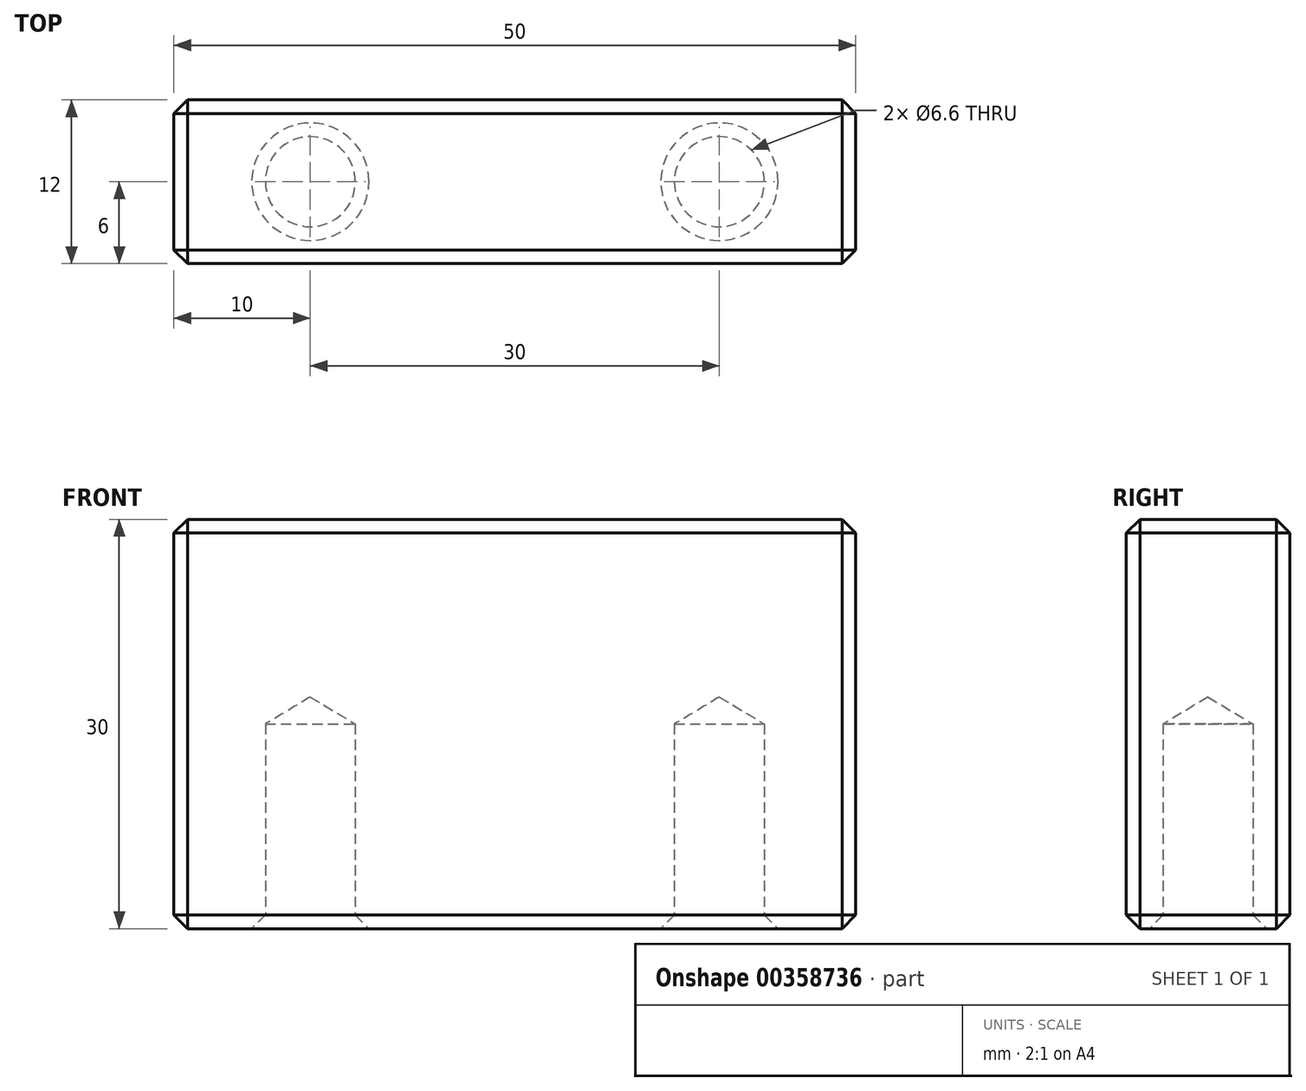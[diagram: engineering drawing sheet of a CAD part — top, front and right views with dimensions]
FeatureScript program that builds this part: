
annotation { "Feature Type Name" : "Feature", "Feature Type Description" : "" }
export const myFeature = defineFeature(function(context is Context, id is Id, definition is map)
    precondition{}
    {
        {
            var Q0;
            Q0=qCreatedBy(makeId("Front.planeOp"),FACE);
            var sketch = newSketch(context, id + "F0", { "sketchPlane" : qUnion([Q0])});
            skLineSegment(sketch, "E0.bottom", {"start": v(25, -15) * mm, "end": v(-25, -15) * mm});
            skLineSegment(sketch, "E0.top", {"start": v(25, 15) * mm, "end": v(-25, 15) * mm});
            skLineSegment(sketch, "E0.left", {"start": v(25, -15) * mm, "end": v(25, 15) * mm});
            skLineSegment(sketch, "E0.right", {"start": v(-25, -15) * mm, "end": v(-25, 15) * mm});
            skPoint(sketch, "E0.middle", {"position": v(0, 0) * mm});
            skSolve(sketch);
        }
        {
            var Q0;
            Q0=makeQuery(id+"F0.imprint","IMPRINT",FACE,{"disambiguationData":[TD([[makeQuery(id+"F0.imprint","IMPRINT",EDGE,{"derivedFrom":sQuery(id+"F0.wireOp",EDGE,"E0.bottom")}),-1.0]])]});
            extrude(context, id + "F1", {"entities" : qUnion([Q0]), "endBound" : BoundingType.SYMMETRIC, "depth" : 12 * mm});
        }
        {
            var Q0;
            Q0=makeQuery(id+"F1.opExtrude","SWEPT_FACE",FACE,{"disambiguationData":[OSD([sQuery(id+"F0.wireOp",EDGE,"E0.bottom")])]});
            var sketch = newSketch(context, id + "F2", { "sketchPlane" : qUnion([Q0])});
            skPoint(sketch, "E1", {"position": v(-15, 0) * mm});
            skPoint(sketch, "E2.MirrorP", {"position": v(15, 0) * mm});
            skSolve(sketch);
        }
        {
            var Q0;
            Q0=sQuery(id+"F2.wireOp",VERTEX,"E1");
            var Q1;
            Q1=sQuery(id+"F2.wireOp",VERTEX,"E2.MirrorP");
            var Q2;
            Q2=makeQuery(id+"F1.opExtrude","SWEPT_BODY",BODY,{"disambiguationData":[OSD([sQuery(id+"F0.wireOp",EDGE,"E0.bottom"),sQuery(id+"F0.wireOp",EDGE,"E0.top"),sQuery(id+"F0.wireOp",EDGE,"E0.left"),sQuery(id+"F0.wireOp",EDGE,"E0.right")])]});
            hole(context, id + "F3", {"style" : HoleStyle.SIMPLE, "endStyle" : HoleEndStyle.BLIND, "standardTappedOrClearance" : lookupTablePath({ "standard" : "ISO", "fit" : "Normal", "size" : "M6", "type" : "Clearance" }), "standardBlindInLast" : lookupTablePath({ "fit" : "Standard", "standard" : "ISO", "size" : "M6", "type" : "Clearance" }), "holeDiameter" : 6.6 * mm, "holeDepth" : 15 * mm, "isTappedThrough" : true, "tappedDepth" : 12 * mm, "tapClearance" : 3, "locations" : qUnion([Q0, Q1]), "scope" : qUnion([Q2])});
        }
        {
            var Q0;
            Q0=makeQuery(id+"F1.opExtrude","CAP_FACE",FACE,{"disambiguationData":[OSD([sQuery(id+"F0.wireOp",EDGE,"E0.bottom"),sQuery(id+"F0.wireOp",EDGE,"E0.top"),sQuery(id+"F0.wireOp",EDGE,"E0.left"),sQuery(id+"F0.wireOp",EDGE,"E0.right")])],"isStart":false});
            var Q1;
            Q1=makeQuery(id+"F1.opExtrude","SWEPT_FACE",FACE,{"disambiguationData":[OSD([sQuery(id+"F0.wireOp",EDGE,"E0.top")])]});
            var Q2;
            Q2=makeQuery(id+"F1.opExtrude","SWEPT_FACE",FACE,{"disambiguationData":[OSD([sQuery(id+"F0.wireOp",EDGE,"E0.left")])]});
            var Q3;
            Q3=makeQuery(id+"F1.opExtrude","CAP_FACE",FACE,{"disambiguationData":[OSD([sQuery(id+"F0.wireOp",EDGE,"E0.bottom"),sQuery(id+"F0.wireOp",EDGE,"E0.top"),sQuery(id+"F0.wireOp",EDGE,"E0.left"),sQuery(id+"F0.wireOp",EDGE,"E0.right")])],"isStart":true});
            var Q4;
            Q4=makeQuery(id+"F1.opExtrude","SWEPT_FACE",FACE,{"disambiguationData":[OSD([sQuery(id+"F0.wireOp",EDGE,"E0.bottom")])]});
            chamfer(context, id + "F4", {"entities" : qUnion([Q0, Q1, Q2, Q3, Q4]), "width" : 1 * mm, "tangentPropagation" : true});
        }
    });
